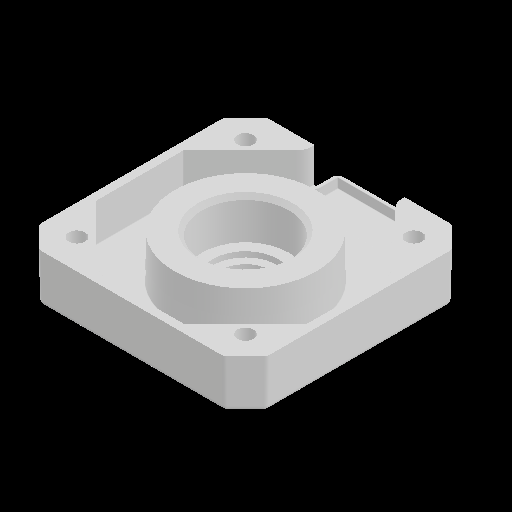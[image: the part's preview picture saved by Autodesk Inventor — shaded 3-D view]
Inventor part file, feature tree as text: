
AUTODESK INVENTOR PART (.ipt)
format: ipt  version: 2023 (Build 270158000, 158)  size: 443,904 bytes
history: native  units: mm
features: fillet x1
ambient origin geometry x8: Origin, YZ Plane, XZ Plane, XY Plane, X Axis, Y Axis, Z Axis, Center Point
bodies: Solid1 (feature_tree)
feature tree (1):
  fillet  "Fillet7"  [1 undecoded]
note: 1 required parameter value undecoded (feature->parameter linkage not recoverable at this tier; creation-order binding heuristic only, values carry confidence <= 0.55)
